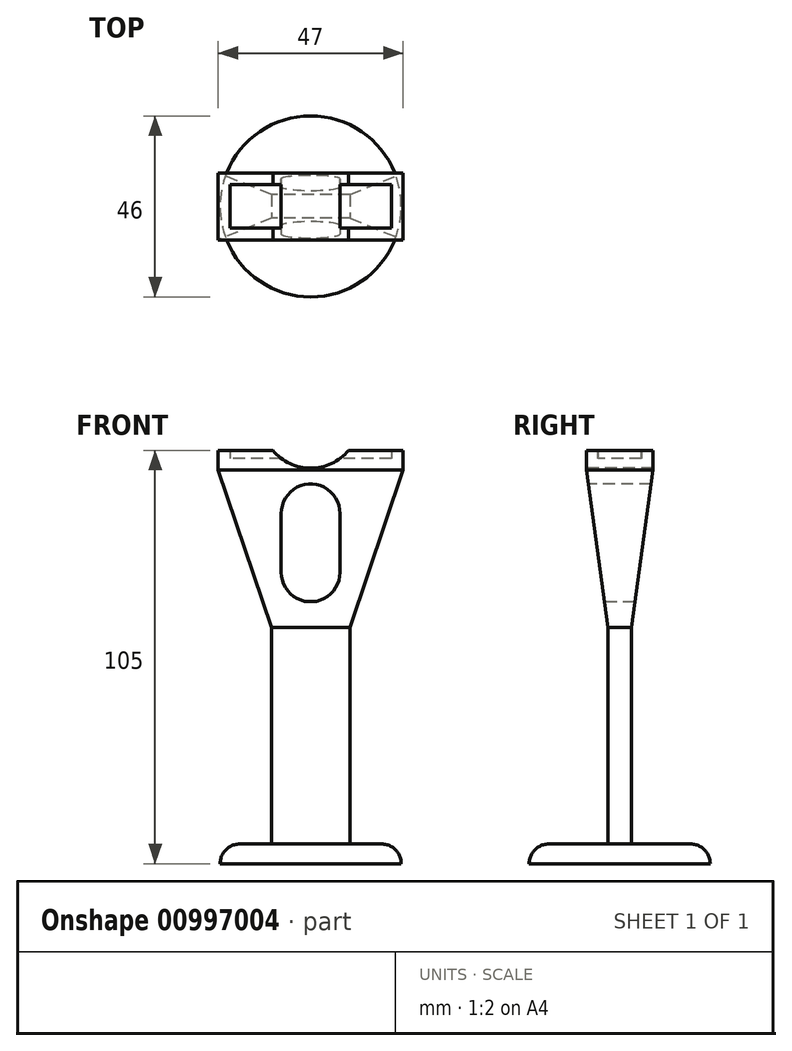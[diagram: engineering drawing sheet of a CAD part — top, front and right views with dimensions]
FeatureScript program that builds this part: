
annotation { "Feature Type Name" : "Feature", "Feature Type Description" : "" }
export const myFeature = defineFeature(function(context is Context, id is Id, definition is map)
    precondition{}
    {
        {
            var Q0;
            Q0=qCreatedBy(makeId("Top.planeOp"),FACE);
            cPlane(context, id + "F0", {"entities" : qUnion([Q0]), "cplaneType" : CPlaneType.OFFSET, "offset" : 100 * mm, "width" : 150 * mm, "height" : 150 * mm});
        }
        {
            var Q0;
            Q0=qCreatedBy(id+"F0.planeOp",FACE);
            var sketch = newSketch(context, id + "F1", { "sketchPlane" : qUnion([Q0])});
            skLineSegment(sketch, "E0.bottom", {"start": v(20.5, 5.5) * mm, "end": v(-20.5, 5.5) * mm});
            skLineSegment(sketch, "E0.top", {"start": v(20.5, -5.5) * mm, "end": v(-20.5, -5.5) * mm});
            skLineSegment(sketch, "E0.left", {"start": v(20.5, 5.5) * mm, "end": v(20.5, -5.5) * mm});
            skLineSegment(sketch, "E0.right", {"start": v(-20.5, 5.5) * mm, "end": v(-20.5, -5.5) * mm});
            skPoint(sketch, "E0.middle", {"position": v(0, 0) * mm});
            skLineSegment(sketch, "E1.bottom", {"start": v(23.5, 8.5) * mm, "end": v(-23.5, 8.5) * mm});
            skLineSegment(sketch, "E1.top", {"start": v(23.5, -8.5) * mm, "end": v(-23.5, -8.5) * mm});
            skLineSegment(sketch, "E1.left", {"start": v(23.5, 8.5) * mm, "end": v(23.5, -8.5) * mm});
            skLineSegment(sketch, "E1.right", {"start": v(-23.5, 8.5) * mm, "end": v(-23.5, -8.5) * mm});
            skSolve(sketch);
        }
        {
            var Q0;
            Q0=makeQuery(id+"F1.imprint","IMPRINT",FACE,{"disambiguationData":[TD([[makeQuery(id+"F1.imprint","IMPRINT",EDGE,{"derivedFrom":sQuery(id+"F1.wireOp",EDGE,"E0.bottom")}),1.0]])]});
            extrude(context, id + "F2", {"entities" : qUnion([Q0]), "depth" : 3 * mm, "offsetDistance" : 25 * mm});
        }
        {
            var Q0;
            Q0 = qSketchRegion(id + "F1", true);
            extrude(context, id + "F3", {"entities" : qUnion([Q0]), "operationType" : NewBodyOperationType.ADD, "depth" : 5 * mm, "offsetDistance" : 25 * mm});
        }
        {
            var Q0;
            Q0=makeQuery(id+"F3.opExtrude","SWEPT_FACE",FACE,{"disambiguationData":[OSD([sQuery(id+"F1.wireOp",EDGE,"E1.top")])]});
            var sketch = newSketch(context, id + "F4", { "sketchPlane" : qUnion([Q0])});
            skLineSegment(sketch, "E2", {"start": v(0, 0) * mm, "end": v(0, 125.21) * mm, "construction": true});
            skCircle(sketch, "E3", {"center": v(0, 113) * mm, "radius": 12.5 * mm});
            skSolve(sketch);
        }
        {
            var Q0;
            {var subQ0=sQuery(id+"F4.wireOp",EDGE,"E3");var subQ1=sQuery(id+"F1.wireOp",EDGE,"E1.top");var subQ2=makeQuery(id+"F4.imprint","INTERSECT",VERTEX,{"derivedFrom":[makeQuery(id+"F3.opExtrude","CAP_EDGE",EDGE,{"disambiguationData":[OSD([subQ1])],"isStart":true}),subQ0]});Q0=makeQuery(id+"F4.imprint","IMPRINT",FACE,{"disambiguationData":[TD([[makeQuery(id+"F4.imprint","IMPRINT",EDGE,{"disambiguationData":[TD([[subQ2,1.0]])],"derivedFrom":subQ0}),1.0]])]});}
            extrude(context, id + "F5", {"entities" : qUnion([Q0]), "operationType" : NewBodyOperationType.REMOVE, "endBound" : BoundingType.THROUGH_ALL, "oppositeDirection" : true, "depth" : 25 * mm, "offsetDistance" : 25 * mm});
        }
        {
            var Q0;
            Q0=qCreatedBy(makeId("Top.planeOp"),FACE);
            var sketch = newSketch(context, id + "F6", { "sketchPlane" : qUnion([Q0])});
            skCircle(sketch, "E4", {"center": v(0, 0) * mm, "radius": 23 * mm});
            skSolve(sketch);
        }
        {
            var Q0;
            Q0=makeQuery(id+"F6.imprint","IMPRINT",FACE,{"disambiguationData":[TD([[makeQuery(id+"F6.imprint","IMPRINT",EDGE,{"derivedFrom":sQuery(id+"F6.wireOp",EDGE,"E4")}),1.0]])]});
            extrude(context, id + "F7", {"entities" : qUnion([Q0]), "depth" : 5 * mm, "offsetDistance" : 25 * mm});
        }
        {
            var Q0;
            Q0=makeQuery(id+"F7.opExtrude","CAP_FACE",FACE,{"disambiguationData":[OSD([sQuery(id+"F6.wireOp",EDGE,"E4")])],"isStart":false});
            var sketch = newSketch(context, id + "F8", { "sketchPlane" : qUnion([Q0])});
            skLineSegment(sketch, "E5.bottom", {"start": v(10, 3) * mm, "end": v(-10, 3) * mm});
            skLineSegment(sketch, "E5.top", {"start": v(10, -3) * mm, "end": v(-10, -3) * mm});
            skLineSegment(sketch, "E5.left", {"start": v(10, 3) * mm, "end": v(10, -3) * mm});
            skLineSegment(sketch, "E5.right", {"start": v(-10, 3) * mm, "end": v(-10, -3) * mm});
            skPoint(sketch, "E5.middle", {"position": v(0, 0) * mm});
            skSolve(sketch);
        }
        {
            var Q0;
            Q0=makeQuery(id+"F8.imprint","IMPRINT",FACE,{"disambiguationData":[TD([[makeQuery(id+"F8.imprint","IMPRINT",EDGE,{"derivedFrom":sQuery(id+"F8.wireOp",EDGE,"E5.bottom")}),1.0]])]});
            var Q1;
            {var subQ0=sQuery(id+"F1.wireOp",EDGE,"E0.right");var subQ1=sQuery(id+"F1.wireOp",EDGE,"E0.left");var subQ2=sQuery(id+"F1.wireOp",EDGE,"E0.top");var subQ3=sQuery(id+"F1.wireOp",EDGE,"E0.bottom");Q1=makeQuery(id+"F3.boolean.opBoolean","MERGE",FACE,{"derivedFrom":[makeQuery(id+"F2.opExtrude","CAP_FACE",FACE,{"disambiguationData":[OSD([subQ3,subQ2,subQ1,subQ0])],"isStart":true}),makeQuery(id+"F3.opExtrude","CAP_FACE",FACE,{"disambiguationData":[OSD([subQ3,subQ2,subQ1,subQ0,sQuery(id+"F1.wireOp",EDGE,"E1.bottom"),sQuery(id+"F1.wireOp",EDGE,"E1.top"),sQuery(id+"F1.wireOp",EDGE,"E1.left"),sQuery(id+"F1.wireOp",EDGE,"E1.right")])],"isStart":true})]});}
            extrude(context, id + "F9", {"entities" : qUnion([Q0]), "operationType" : NewBodyOperationType.ADD, "depth" : 55 * mm, "endBoundEntityFace" : qUnion([Q1]), "offsetDistance" : 25 * mm});
        }
        {
            var Q0;
            Q0=makeQuery(id+"F9.opExtrude","CAP_FACE",FACE,{"disambiguationData":[OSD([sQuery(id+"F8.wireOp",EDGE,"E5.bottom"),sQuery(id+"F8.wireOp",EDGE,"E5.top"),sQuery(id+"F8.wireOp",EDGE,"E5.left"),sQuery(id+"F8.wireOp",EDGE,"E5.right")])],"isStart":false});
            var Q1;
            {var subQ0=sQuery(id+"F1.wireOp",EDGE,"E0.right");var subQ1=sQuery(id+"F1.wireOp",EDGE,"E0.left");var subQ2=sQuery(id+"F1.wireOp",EDGE,"E0.top");var subQ3=sQuery(id+"F1.wireOp",EDGE,"E0.bottom");Q1=makeQuery(id+"F3.boolean.opBoolean","MERGE",FACE,{"derivedFrom":[makeQuery(id+"F2.opExtrude","CAP_FACE",FACE,{"disambiguationData":[OSD([subQ3,subQ2,subQ1,subQ0])],"isStart":true}),makeQuery(id+"F3.opExtrude","CAP_FACE",FACE,{"disambiguationData":[OSD([subQ3,subQ2,subQ1,subQ0,sQuery(id+"F1.wireOp",EDGE,"E1.bottom"),sQuery(id+"F1.wireOp",EDGE,"E1.top"),sQuery(id+"F1.wireOp",EDGE,"E1.left"),sQuery(id+"F1.wireOp",EDGE,"E1.right")])],"isStart":true})]});}
            loft(context, id + "F10", {"sheetProfilesArray" : [{ "sheetProfileEntities" : qUnion([Q0]) }, { "sheetProfileEntities" : qUnion([Q1]) }]});
        }
        {
            var Q0;
            Q0=qCreatedBy(makeId("Front.planeOp"),FACE);
            var sketch = newSketch(context, id + "F11", { "sketchPlane" : qUnion([Q0])});
            skLineSegment(sketch, "E6", {"start": v(0, 89) * mm, "end": v(0, 74) * mm});
            skArc(sketch, "E7.0.startCap", {"start": v(-7.5, 89) * mm, "mid": v(0, 96.5) * mm, "end": v(7.5, 89) * mm});
            skArc(sketch, "E7.0.endCap", {"start": v(7.5, 74) * mm, "mid": v(0, 66.5) * mm, "end": v(-7.5, 74) * mm});
            skLineSegment(sketch, "E7.0.left", {"start": v(7.5, 89) * mm, "end": v(7.5, 74) * mm});
            skLineSegment(sketch, "E7.0.right", {"start": v(-7.5, 89) * mm, "end": v(-7.5, 74) * mm});
            skSolve(sketch);
        }
        {
            var Q0;
            Q0 = qSketchRegion(id + "F11", true);
            extrude(context, id + "F12", {"entities" : qUnion([Q0]), "operationType" : NewBodyOperationType.REMOVE, "endBound" : BoundingType.SYMMETRIC, "oppositeDirection" : true, "depth" : 50 * mm, "offsetDistance" : 25 * mm});
        }
        {
            var Q0;
            Q0=makeQuery(id+"F9.opExtrude","CAP_EDGE",EDGE,{"disambiguationData":[OSD([sQuery(id+"F8.wireOp",EDGE,"E5.top")])],"isStart":true});
            var Q1;
            Q1=makeQuery(id+"F9.opExtrude","CAP_EDGE",EDGE,{"disambiguationData":[OSD([sQuery(id+"F8.wireOp",EDGE,"E5.right")])],"isStart":true});
            var Q2;
            Q2=makeQuery(id+"F9.opExtrude","CAP_EDGE",EDGE,{"disambiguationData":[OSD([sQuery(id+"F8.wireOp",EDGE,"E5.bottom")])],"isStart":true});
            var Q3;
            Q3=makeQuery(id+"F9.opExtrude","CAP_EDGE",EDGE,{"disambiguationData":[OSD([sQuery(id+"F8.wireOp",EDGE,"E5.left")])],"isStart":true});
            var Q4;
            Q4=makeQuery(id+"F7.opExtrude","CAP_EDGE",EDGE,{"disambiguationData":[OSD([sQuery(id+"F6.wireOp",EDGE,"E4")])],"isStart":false});
            fillet(context, id + "F13", {"entities" : qUnion([Q0, Q1, Q2, Q3, Q4]), "radius" : 5 * mm, "tangentPropagation" : true, "allowEdgeOverflow" : false});
        }
    });
